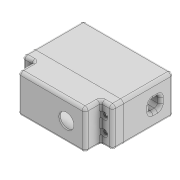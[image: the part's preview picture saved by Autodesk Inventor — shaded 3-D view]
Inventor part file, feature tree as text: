
AUTODESK INVENTOR PART (.ipt)
format: ipt  version: 2021 (Build 250183000, 183)  size: 495,104 bytes
history: native  units: mm
features: sketch x9, other x5, hole x5, extrude x4, mirror x4, fillet x2, projected_geometry x1
ambient origin geometry x8: Origin, YZ Plane, XZ Plane, XY Plane, X Axis, Y Axis, Z Axis, Center Point
bodies: Body1 (feature_tree), Body2 (feature_tree)
feature tree (30):
  other  "Твердое тело1"
  extrude  "Выдавливание1"  Depth=40.4mm
  extrude  "Выдавливание2"  Depth=40.0mm
  mirror  "Зеркальное отражение1"
  extrude  "Выдавливание3"  Depth=27.7mm
  mirror  "Зеркальное отражение2"
  hole  "Отверстие1"  [1 undecoded]
  hole  "Отверстие2"  [1 undecoded]
  mirror  "Зеркальное отражение4"
  other  "РабПлоскость1"
  fillet  "Сопряжение2"  Radius=1.9mm
  other  "Разделение1"
  hole  "Отверстие3"  [1 undecoded]
  mirror  "Зеркальное отражение3"
  extrude  "Выдавливание4"  Depth=5.9mm
  fillet  "Сопряжение3"  Radius=1.7mm
  hole  "Отверстие4"  [1 undecoded]
  hole  "Отверстие5"  [1 undecoded]
  sketch  "Эскиз1"
  sketch  "Эскиз2"
  sketch  "Эскиз3"
  sketch  "Эскиз4"
  sketch  "Эскиз5"
  sketch  "Эскиз6"
  sketch  "Эскиз7"
  projected_geometry  "Спроецированная петля1"
  sketch  "Эскиз8"
  sketch  "Эскиз9"
  other  "Твердое тело2"
  other  "Твердое тело3"
note: 5 required parameter values undecoded (feature->parameter linkage not recoverable at this tier; creation-order binding heuristic only, values carry confidence <= 0.55)
